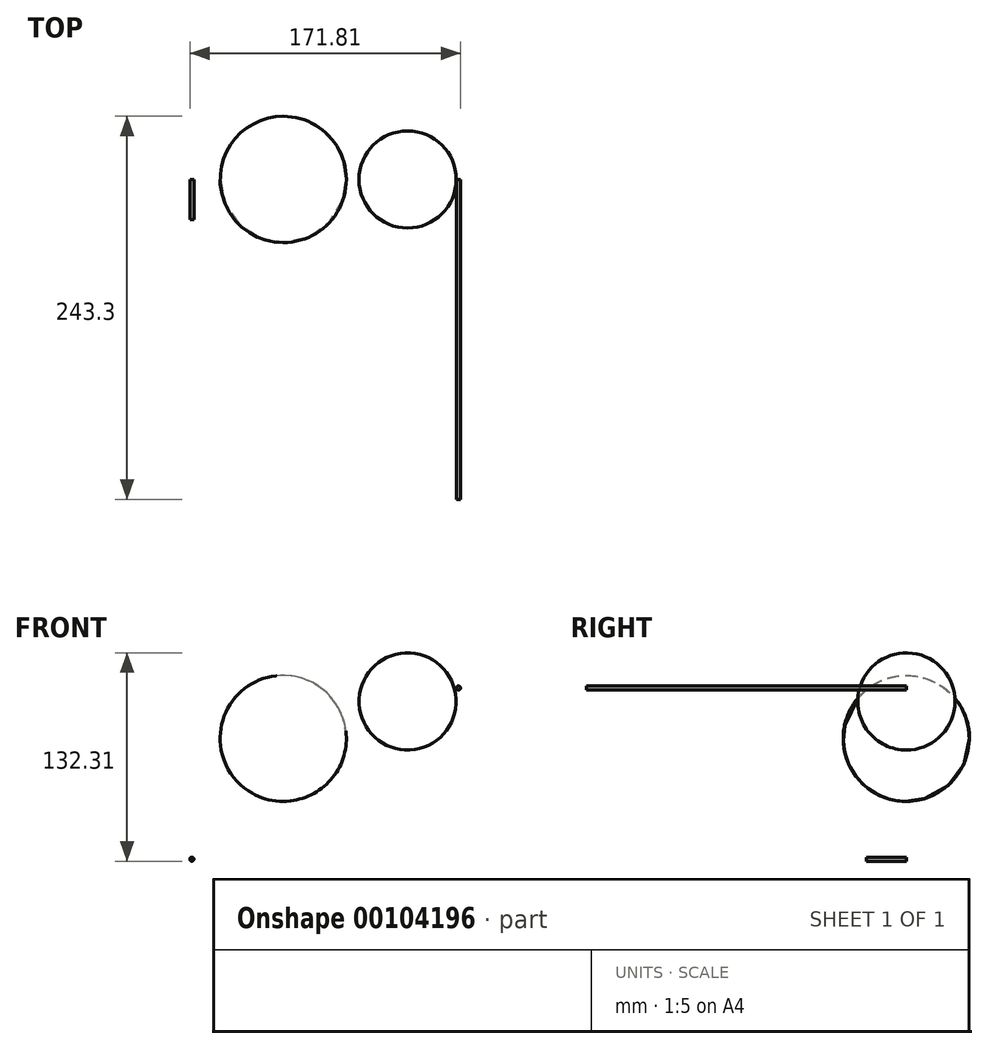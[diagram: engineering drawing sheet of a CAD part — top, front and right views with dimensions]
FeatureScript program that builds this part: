
annotation { "Feature Type Name" : "Feature", "Feature Type Description" : "" }
export const myFeature = defineFeature(function(context is Context, id is Id, definition is map)
    precondition{}
    {
        {
            var Q0;
            Q0=qCreatedBy(makeId("Front.planeOp"),FACE);
            var sketch = newSketch(context, id + "F0", { "sketchPlane" : qUnion([Q0])});
            skCircle(sketch, "E0", {"center": v(-63.6, 25.81) * mm, "radius": 1.24 * mm});
            skSolve(sketch);
        }
        {
            var Q0;
            Q0=makeQuery(id+"F0.imprint","IMPRINT",FACE,{"disambiguationData":[TD([[makeQuery(id+"F0.imprint","IMPRINT",EDGE,{"derivedFrom":sQuery(id+"F0.wireOp",EDGE,"E0")}),1.0]])]});
            extrude(context, id + "F1", {"entities" : qUnion([Q0]), "depth" : 203.2 * mm});
        }
        {
            var Q0;
            Q0=qCreatedBy(makeId("Front.planeOp"),FACE);
            var sketch = newSketch(context, id + "F2", { "sketchPlane" : qUnion([Q0])});
            skCircle(sketch, "E1", {"center": v(-232.93, -82.95) * mm, "radius": 1.24 * mm});
            skSolve(sketch);
        }
        {
            var Q0;
            Q0=makeQuery(id+"F2.imprint","IMPRINT",FACE,{"disambiguationData":[TD([[makeQuery(id+"F2.imprint","IMPRINT",EDGE,{"derivedFrom":sQuery(id+"F2.wireOp",EDGE,"E1")}),1.0]])]});
            extrude(context, id + "F3", {"entities" : qUnion([Q0]), "depth" : 25.4 * mm});
        }
        {
            var Q0;
            Q0=qCreatedBy(makeId("Front.planeOp"),FACE);
            var sketch = newSketch(context, id + "F4", { "sketchPlane" : qUnion([Q0])});
            skArc(sketch, "E2", {"start": v(-170.34, -45.92) * mm, "mid": v(-135.08, -1.59) * mm, "end": v(-179.5, 33.56) * mm});
            skLineSegment(sketch, "E3", {"start": v(-179.5, 33.56) * mm, "end": v(-170.34, -45.92) * mm});
            skSolve(sketch);
        }
        {
            var Q0;
            Q0=makeQuery(id+"F4.imprint","IMPRINT",FACE,{"disambiguationData":[TD([[makeQuery(id+"F4.imprint","IMPRINT",EDGE,{"derivedFrom":sQuery(id+"F4.wireOp",EDGE,"E2")}),1.0]])]});
            var Q1;
            Q1=sQuery(id+"F4.wireOp",EDGE,"E3");
            revolve(context, id + "F5", {"entities" : qUnion([Q0]), "axis" : qUnion([Q1]), "revolveType" : RevolveType.FULL});
        }
        {
            var Q0;
            Q0=qCreatedBy(makeId("Front.planeOp"),FACE);
            var sketch = newSketch(context, id + "F6", { "sketchPlane" : qUnion([Q0])});
            skCircle(sketch, "E4", {"center": v(-95.93, 17.26) * mm, "radius": 30.86 * mm});
            skLineSegment(sketch, "E5", {"start": v(-97.42, 48.09) * mm, "end": v(-94.43, -13.56) * mm});
            skSolve(sketch);
        }
        {
            var Q0;
            {var subQ0=sQuery(id+"F6.wireOp",EDGE,"E5");Q0=makeQuery(id+"F6.imprint","IMPRINT",FACE,{"disambiguationData":[TD([[makeQuery(id+"F6.imprint","IMPRINT",EDGE,{"derivedFrom":subQ0}),1.0]])]});}
            var Q1;
            Q1=sQuery(id+"F6.wireOp",EDGE,"E5");
            revolve(context, id + "F7", {"entities" : qUnion([Q0]), "axis" : qUnion([Q1]), "revolveType" : RevolveType.FULL});
        }
    });
